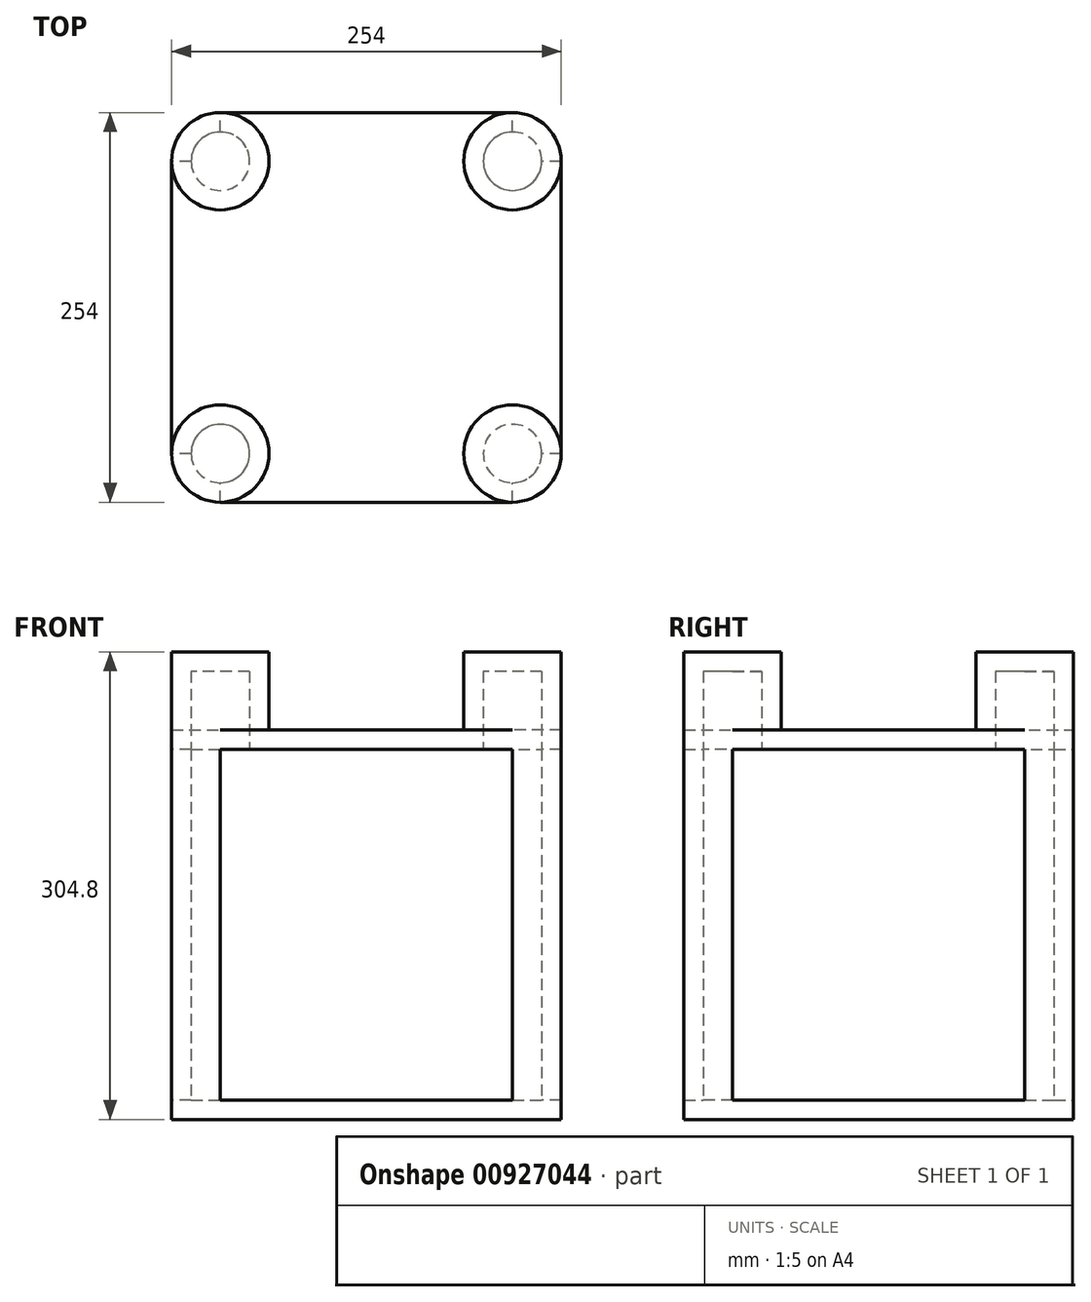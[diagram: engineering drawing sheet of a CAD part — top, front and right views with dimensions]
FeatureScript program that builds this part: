
annotation { "Feature Type Name" : "Feature", "Feature Type Description" : "" }
export const myFeature = defineFeature(function(context is Context, id is Id, definition is map)
    precondition{}
    {
        {
            var Q0;
            Q0=qCreatedBy(makeId("Top.planeOp"),FACE);
            var sketch = newSketch(context, id + "F0", { "sketchPlane" : qUnion([Q0])});
            skLineSegment(sketch, "E0.bottom", {"start": v(127, 127) * mm, "end": v(-127, 127) * mm});
            skLineSegment(sketch, "E0.top", {"start": v(127, -127) * mm, "end": v(-127, -127) * mm});
            skLineSegment(sketch, "E0.left", {"start": v(127, 127) * mm, "end": v(127, -127) * mm});
            skLineSegment(sketch, "E0.right", {"start": v(-127, 127) * mm, "end": v(-127, -127) * mm});
            skPoint(sketch, "E0.middle", {"position": v(0, 0) * mm});
            skCircle(sketch, "E1", {"center": v(-95.25, 95.25) * mm, "radius": 31.75 * mm});
            skCircle(sketch, "E2", {"center": v(95.25, 95.25) * mm, "radius": 31.75 * mm});
            skCircle(sketch, "E3", {"center": v(-95.25, -95.25) * mm, "radius": 31.75 * mm});
            skCircle(sketch, "E4", {"center": v(95.25, -95.25) * mm, "radius": 31.75 * mm});
            skSolve(sketch);
        }
        {
            var Q0;
            {var subQ5=sQuery(id+"F0.wireOp",EDGE,"E2");var subQ13=sQuery(id+"F0.wireOp",EDGE,"E0.bottom");var subQ14=makeQuery(id+"F0.imprint","INTERSECT",VERTEX,{"derivedFrom":[subQ13,subQ5]});Q0=makeQuery(id+"F0.imprint","IMPRINT",FACE,{"disambiguationData":[TD([[makeQuery(id+"F0.imprint","IMPRINT",EDGE,{"disambiguationData":[TD([[subQ14,-1.0]])],"derivedFrom":subQ13}),1.0]])]});}
            extrude(context, id + "F1", {"entities" : qUnion([Q0]), "depth" : 254 * mm, "offsetDistance" : 25.4 * mm});
        }
        {
            var Q0;
            {var subQ0=sQuery(id+"F0.wireOp",EDGE,"E3");var subQ1=makeQuery(id+"F0.imprint","INTERSECT",VERTEX,{"derivedFrom":[sQuery(id+"F0.wireOp",EDGE,"E0.top"),subQ0]});Q0=makeQuery(id+"F0.imprint","IMPRINT",FACE,{"disambiguationData":[TD([[makeQuery(id+"F0.imprint","IMPRINT",EDGE,{"disambiguationData":[TD([[subQ1,1.0]])],"derivedFrom":subQ0}),1.0]])]});}
            var Q1;
            {var subQ0=sQuery(id+"F0.wireOp",EDGE,"E4");var subQ1=makeQuery(id+"F0.imprint","INTERSECT",VERTEX,{"derivedFrom":[sQuery(id+"F0.wireOp",EDGE,"E0.top"),subQ0]});Q1=makeQuery(id+"F0.imprint","IMPRINT",FACE,{"disambiguationData":[TD([[makeQuery(id+"F0.imprint","IMPRINT",EDGE,{"disambiguationData":[TD([[subQ1,1.0]])],"derivedFrom":subQ0}),1.0]])]});}
            var Q2;
            {var subQ0=sQuery(id+"F0.wireOp",EDGE,"E2");var subQ1=makeQuery(id+"F0.imprint","INTERSECT",VERTEX,{"derivedFrom":[sQuery(id+"F0.wireOp",EDGE,"E0.bottom"),subQ0]});Q2=makeQuery(id+"F0.imprint","IMPRINT",FACE,{"disambiguationData":[TD([[makeQuery(id+"F0.imprint","IMPRINT",EDGE,{"disambiguationData":[TD([[subQ1,1.0]])],"derivedFrom":subQ0}),1.0]])]});}
            var Q3;
            {var subQ0=sQuery(id+"F0.wireOp",EDGE,"E1");var subQ1=makeQuery(id+"F0.imprint","INTERSECT",VERTEX,{"derivedFrom":[sQuery(id+"F0.wireOp",EDGE,"E0.bottom"),subQ0]});Q3=makeQuery(id+"F0.imprint","IMPRINT",FACE,{"disambiguationData":[TD([[makeQuery(id+"F0.imprint","IMPRINT",EDGE,{"disambiguationData":[TD([[subQ1,-1.0]])],"derivedFrom":subQ0}),1.0]])]});}
            extrude(context, id + "F2", {"entities" : qUnion([Q0, Q1, Q2, Q3]), "operationType" : NewBodyOperationType.ADD, "depth" : 304.8 * mm, "offsetDistance" : 25.4 * mm});
        }
        {
            var Q0;
            Q0=makeQuery(id+"F1.opExtrude","SWEPT_FACE",FACE,{"disambiguationData":[OSD([sQuery(id+"F0.wireOp",EDGE,"E0.top")])]});
            var Q1;
            Q1=makeQuery(id+"F1.opExtrude","SWEPT_FACE",FACE,{"disambiguationData":[OSD([sQuery(id+"F0.wireOp",EDGE,"E0.right")])]});
            var Q2;
            Q2=makeQuery(id+"F1.opExtrude","SWEPT_FACE",FACE,{"disambiguationData":[OSD([sQuery(id+"F0.wireOp",EDGE,"E0.bottom")])]});
            var Q3;
            Q3=makeQuery(id+"F1.opExtrude","SWEPT_FACE",FACE,{"disambiguationData":[OSD([sQuery(id+"F0.wireOp",EDGE,"E0.left")])]});
            shell(context, id + "F3", {"entities" : qUnion([Q0, Q1, Q2, Q3]), "thickness" : 12.7 * mm});
        }
    });
